# Revit family: IS_Finesse_E3406_BIM_NL
name_source: partatom
category: Plumbing Fixtures
units: mm (PartAtom-declared; Revit-internal decimal feet)

## family parameters
Cut with Voids When Loaded = No
Host = Face
Maintain Annotation Orientation = No
OmniClass Number = 23.45.05.14.21.11
OmniClass Title = Bath/Shower Units
Part Type = Normal
Room Calculation Point = No
Round Connector Dimension = Use Diameter
Shared = Yes

## types (6) — shared parameters
Accessories = https://www.idealstandard.nl
Afmetingen = 480 x 409 x 370mm
AfstandsEenheid = millimeter
AreaUnits = millimeters
Artikelomschrijving = FINESSE | Wastafelmeubel 480x409x370 mm, 1 lade
Assembly Code = C1030200
AssetType = Fixed
Auteur = Ideal Standard
BIMObjectName = ISI_IdealStandard_Furniture_Finesse_E3406
BREEAM = No
Beschrijvinggarantie = Fabrieksgarantie
BimObjectNaam = ISI_IdealStandard_Furniture_Finesse_E3406
Brand = Ideal Standard
Breedte = 480
ConnectionType = Plumbing
CurrencyUnit = €
Default Elevation = 1219 mm
Description = FINESSE | Basin unit 480x409x370 mm, 1 drawer
Diepte = 408,746001958394
DurationUnit = year
DuurEenheid = jaar
ECA = No
EPD = https://www.idealstandard.nl
ExpectedLife = 30
Garantieunits = Jaar
GemaaktOp = 2024/09/04
Help = https://www.idealstandard.nl
Hoogte = 370
Hulp = https://www.idealstandard.nl
IfcExportAs = IfcFurnitureType
Installatieinstructies = https://www.idealstandard.nl
InstallationInstructions = https://www.idealstandard.nl
Lengte = 408,746001958394
LinearUnits = millimeters
Manufacturer = Ideal Standard
ManufacturerURL = https://www.idealstandard.nl
Materiaal = hout
Merk = Ideal Standard
ModelReference = FINESSE | Basin unit 480x409x370 mm, 1 drawer
NBSDescription = Baths
Name = ISI_Furniture_Finesse_E3406_IdealStandard
NominalDepth = 409 mm  [stored 1.34186 ft]
NominalHeight = 370 mm  [stored 1.21391 ft]
NominalLength = 409 mm  [stored 1.34186 ft]
NominalWidth = 480 mm  [stored 1.5748 ft]
ProductInformation = https://www.idealstandard.nl
ProductSoort = Meubilair
Productinformatie = https://www.idealstandard.nl
Shape = Rectangular
Size = 480 x 409 x 370mm
Space = Internal
SpareParts = https://www.idealstandard.nl
TMV3 = No
Telefoonnummer = 077 355 08 08
Typeconnectie = Sanitair
URL = https://www.idealstandard.nl
Uniclass2015Code = Pr_40_20_76
Uniclass2015Title = Sanitary accessories
Uniclass2015Version = Products v1.34
Urlproducent = https://www.idealstandard.nl
ValutaEenheid = €
Versie = 1
Version = 1
VolumeUnits = Litres
Volumeunits = Liter
Vorm = Rechthoekig
WRAS = No
WarrantyDescription = Manufacturers Warranty
WarrantyDurationParts = 25
WarrantyDurationUnit = year
WarrantyGuarantorParts = https://www.idealstandard.nl
WaterEfficientProduct = No
Wisselstukken = https://www.idealstandard.nl
zero-valued in all types: Vervangingskosten

## per-type parameters (varying)
| type | Afwerking | Artikelnummer | Artikelreferentie | BarCode | Color | Eigenschappen | Features | Finish | Kleur | MAT | Model | ModelNumber | NettWeight | Nettogewicht |
| E3406UP - FINESSE BSN UN C.AIR CUBE 55 1DRW GEMT | Greige mat | E3406UP | FINESSE / Wastafelmeubel 480x409x370 mm in mat greige afwerking, 1 lade / Volledige extractielade, Softclose, Ruimtebesparend, Voorgemonteerd, Duurzaam geproduceerd hout | 5017830566250 | greige matt | FINESSE / Wastafelmeubel 480x409x370 mm in mat greige afwerking, 1 lade / Volledige extractielade, Softclose, Ruimtebesparend, Voorgemonteerd, Duurzaam geproduceerd hout | FINESSE / Basin unit 480x409x370 mm in greige matt finish, 1 drawer / Full extraction drawer, Soft close, Space saving, Assembled, Sustainably sourced wood | greige matt | Greige mat | UP | E3406UP | E3406UP | 13.46 Kg | 13.46 Kg |
| E3406UQ - FINESSE BSN UN C.AIR CUBE 55 1DRW ABMT | Mat asblauw | E3406UQ | FINESSE / Wastafelmeubel 480x409x370 mm in matt ashblue afwerking, 1 lade / Volledige extractielade, Softclose, Ruimtebesparend, Voorgemonteerd, Duurzaam geproduceerd hout | 5017830566267 | matt ashblue | FINESSE / Wastafelmeubel 480x409x370 mm in matt ashblue afwerking, 1 lade / Volledige extractielade, Softclose, Ruimtebesparend, Voorgemonteerd, Duurzaam geproduceerd hout | FINESSE / Basin unit 480x409x370 mm in matt ashblue finish, 1 drawer / Full extraction drawer, Soft close, Space saving, Assembled, Sustainably sourced wood | matt ashblue | Mat asblauw | UQ | E3406UQ | E3406UQ | 13.08 Kg | 13.08 Kg |
| E3406UR - FINESSE BSN UN C.AIR CUBE 55 1DRW DKEM | Donkere iep | E3406UR | FINESSE / Wastafelmeubel 480x409x370 mm in dark elm afwerking, 1 lade / Volledige extractielade, Softclose, Ruimtebesparend, Voorgemonteerd, Duurzaam geproduceerd hout | 5017830566274 | dark elm | FINESSE / Wastafelmeubel 480x409x370 mm in dark elm afwerking, 1 lade / Volledige extractielade, Softclose, Ruimtebesparend, Voorgemonteerd, Duurzaam geproduceerd hout | FINESSE / Basin unit 480x409x370 mm in dark elm finish, 1 drawer / Full extraction drawer, Soft close, Space saving, Assembled, Sustainably sourced wood | dark elm | Donkere iep | UR | E3406UR | E3406UR | 12.48 Kg | 12.48 Kg |
| E3406US - FINESSE BSN UN C.AIR CUBE 55 1DRW WOAK | Witte eik | E3406US | FINESSE / Wastafelmeubel 480x409x370 mm in white oak afwerking, 1 lade / Volledige extractielade, Softclose, Ruimtebesparend, Voorgemonteerd, Duurzaam geproduceerd hout | 5017830566281 | white oak | FINESSE / Wastafelmeubel 480x409x370 mm in white oak afwerking, 1 lade / Volledige extractielade, Softclose, Ruimtebesparend, Voorgemonteerd, Duurzaam geproduceerd hout | FINESSE / Basin unit 480x409x370 mm in white oak finish, 1 drawer / Full extraction drawer, Soft close, Space saving, Assembled, Sustainably sourced wood | white oak | Witte eik | US | E3406US | E3406US | 12.93 Kg | 12.93 Kg |
| E3406Y1 - FINESSE BSN UN C.AIR CUBE 55 1DRW WHMT | Mat wit | E3406Y1 | FINESSE / Wastafelmeubel 480x409x370 mm in matt white afwerking, 1 lade / Volledige extractielade, Softclose, Ruimtebesparend, Voorgemonteerd, Duurzaam geproduceerd hout | 5017830566298 | matt white | FINESSE / Wastafelmeubel 480x409x370 mm in matt white afwerking, 1 lade / Volledige extractielade, Softclose, Ruimtebesparend, Voorgemonteerd, Duurzaam geproduceerd hout | FINESSE / Basin unit 480x409x370 mm in matt white finish, 1 drawer / Full extraction drawer, Soft close, Space saving, Assembled, Sustainably sourced wood | matt white | Mat wit | Y1 | E3406Y1 | E3406Y1 | 13.46 Kg | 13.46 Kg |
| E3406Y2 - FINESSE BSN UN C.AIR CUBE 55 1DRW ANMT | Mat antraciet | E3406Y2 | FINESSE / Wastafelmeubel 480x409x370 mm in matt anthracite afwerking, 1 lade / Volledige extractielade, Softclose, Ruimtebesparend, Voorgemonteerd, Duurzaam geproduceerd hout | 5017830566304 | matt anthracite | FINESSE / Wastafelmeubel 480x409x370 mm in matt anthracite afwerking, 1 lade / Volledige extractielade, Softclose, Ruimtebesparend, Voorgemonteerd, Duurzaam geproduceerd hout | FINESSE / Basin unit 480x409x370 mm in matt anthracite finish, 1 drawer / Full extraction drawer, Soft close, Space saving, Assembled, Sustainably sourced wood | matt anthracite | Mat antraciet | Y2 | E3406Y2 | E3406Y2 | 13.46 Kg | 13.46 Kg |

note: [stored X ft] marks values corroborated as IEEE doubles in the binary element streams (Revit-internal decimal feet)

## geometry (parser evidence)
native form markers: Sweep x3
no freeform markers — native parametric forms only
